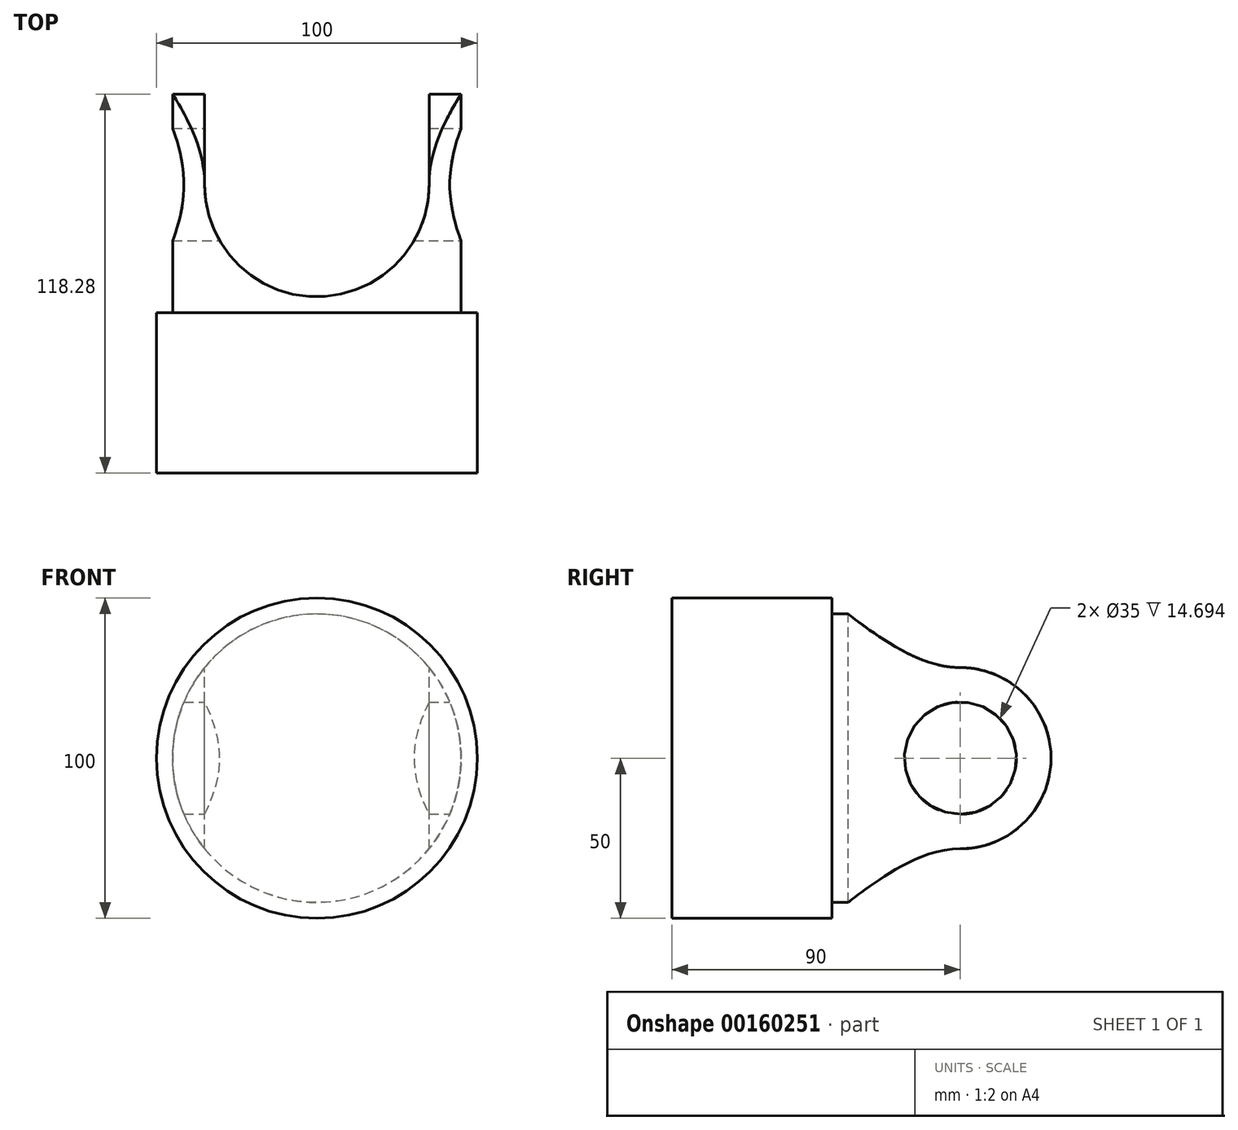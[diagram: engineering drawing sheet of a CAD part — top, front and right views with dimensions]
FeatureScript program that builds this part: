
annotation { "Feature Type Name" : "Feature", "Feature Type Description" : "" }
export const myFeature = defineFeature(function(context is Context, id is Id, definition is map)
    precondition{}
    {
        {
            var Q0;
            Q0=qCreatedBy(makeId("Front.planeOp"),FACE);
            var sketch = newSketch(context, id + "F0", { "sketchPlane" : qUnion([Q0])});
            skCircle(sketch, "E0", {"center": v(0, 0) * mm, "radius": 50 * mm});
            skSolve(sketch);
        }
        {
            var Q0;
            Q0=qSketchRegion(id+"F0",true);
            extrude(context, id + "F1", {"entities" : qUnion([Q0]), "oppositeDirection" : true, "depth" : 50 * mm});
        }
        {
            var Q0;
            Q0=makeQuery(id+"F1.opExtrude","CAP_FACE",FACE,{"disambiguationData":[OSD([sQuery(id+"F0.wireOp",EDGE,"E0")])],"isStart":false});
            var sketch = newSketch(context, id + "F2", { "sketchPlane" : qUnion([Q0])});
            skCircle(sketch, "E1", {"center": v(0, 0) * mm, "radius": 45 * mm});
            skSolve(sketch);
        }
        {
            var Q0;
            Q0=qSketchRegion(id+"F2",true);
            extrude(context, id + "F3", {"entities" : qUnion([Q0]), "operationType" : NewBodyOperationType.ADD, "depth" : 80 * mm});
        }
        {
            var Q0;
            Q0=qCreatedBy(makeId("Top.planeOp"),FACE);
            var sketch = newSketch(context, id + "F4", { "sketchPlane" : qUnion([Q0])});
            skCircle(sketch, "E2", {"center": v(0, 90) * mm, "radius": 35 * mm});
            skLineSegment(sketch, "E3", {"start": v(35, 90) * mm, "end": v(35, 130) * mm});
            skPoint(sketch, "E4", {"position": v(-35, 90) * mm});
            skLineSegment(sketch, "E5", {"start": v(-35, 90) * mm, "end": v(-35, 130) * mm});
            skLineSegment(sketch, "E6", {"start": v(-35, 130) * mm, "end": v(35, 130) * mm});
            skSolve(sketch);
        }
        {
            var Q0;
            Q0=qSketchRegion(id+"F4",true);
            extrude(context, id + "F5", {"entities" : qUnion([Q0]), "operationType" : NewBodyOperationType.REMOVE, "endBound" : BoundingType.SYMMETRIC, "oppositeDirection" : true, "depth" : 200 * mm});
        }
        {
            var Q0;
            Q0=makeQuery(id+"F5.boolean.opBoolean","COPY",FACE,{"derivedFrom":makeQuery(id+"F5.opExtrude","SWEPT_FACE",FACE,{"disambiguationData":[OSD([sQuery(id+"F4.wireOp",EDGE,"E5")])]})});
            var sketch = newSketch(context, id + "F6", { "sketchPlane" : qUnion([Q0])});
            skCircle(sketch, "E7", {"center": v(90, 0) * mm, "radius": 17.5 * mm});
            skArc(sketch, "E8", {"start": v(90, -28.28) * mm, "mid": v(118.28, 0) * mm, "end": v(90, 28.28) * mm});
            skLineSegment(sketch, "E9", {"start": v(90, 28.28) * mm, "end": v(130, 28.28) * mm});
            skLineSegment(sketch, "E10", {"start": v(130, 28.28) * mm, "end": v(130, -28.28) * mm});
            skLineSegment(sketch, "E11", {"start": v(130, -28.28) * mm, "end": v(90, -28.28) * mm});
            skSolve(sketch);
        }
        {
            var Q0;
            Q0=qSketchRegion(id+"F6",true);
            extrude(context, id + "F7", {"entities" : qUnion([Q0]), "operationType" : NewBodyOperationType.REMOVE, "endBound" : BoundingType.SYMMETRIC, "oppositeDirection" : true, "depth" : 200 * mm});
        }
    });
